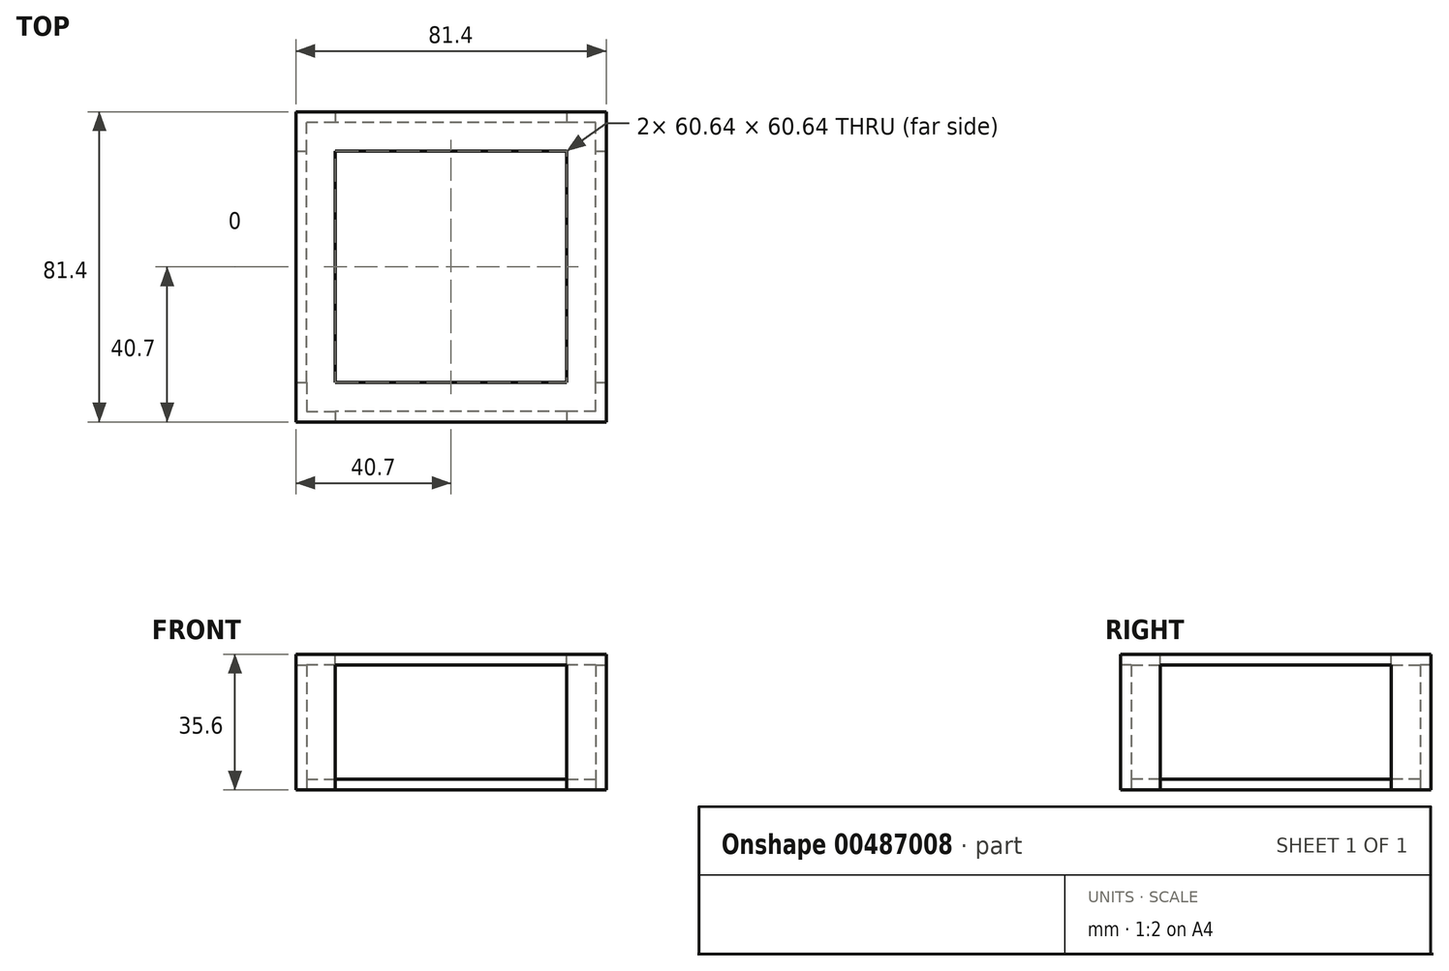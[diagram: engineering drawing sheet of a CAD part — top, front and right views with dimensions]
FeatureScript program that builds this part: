
annotation { "Feature Type Name" : "Feature", "Feature Type Description" : "" }
export const myFeature = defineFeature(function(context is Context, id is Id, definition is map)
    precondition{}
    {
        {
            assignVariable(context, id + "F0", {"name" : "Grosor", "anyValue" : 2.8});
        }
        {
            assignVariable(context, id + "F1", {"name" : "Alto", "anyValue" : 30});
        }
        {
            var Q0;
            Q0=qCreatedBy(makeId("Top.planeOp"),FACE);
            var sketch = newSketch(context, id + "F2", { "sketchPlane" : qUnion([Q0])});
            skLineSegment(sketch, "E0.bottom", {"start": v(37.9, -37.9) * mm, "end": v(-37.9, -37.9) * mm});
            skLineSegment(sketch, "E0.top", {"start": v(37.9, 37.9) * mm, "end": v(-37.9, 37.9) * mm});
            skLineSegment(sketch, "E0.left", {"start": v(37.9, -37.9) * mm, "end": v(37.9, 37.9) * mm});
            skLineSegment(sketch, "E0.right", {"start": v(-37.9, -37.9) * mm, "end": v(-37.9, 37.9) * mm});
            skPoint(sketch, "E0.middle", {"position": v(0, 0) * mm});
            skLineSegment(sketch, "E1.0", {"start": v(40.7, 40.7) * mm, "end": v(-40.7, 40.7) * mm});
            skLineSegment(sketch, "E1.1", {"start": v(40.7, -40.7) * mm, "end": v(40.7, 40.7) * mm});
            skLineSegment(sketch, "E1.2", {"start": v(40.7, -40.7) * mm, "end": v(-40.7, -40.7) * mm});
            skLineSegment(sketch, "E1.3", {"start": v(-40.7, -40.7) * mm, "end": v(-40.7, 40.7) * mm});
            skLineSegment(sketch, "E2.bottom", {"start": v(-30.32, 40.7) * mm, "end": v(30.32, 40.7) * mm});
            skLineSegment(sketch, "E2.top", {"start": v(-30.32, -40.7) * mm, "end": v(30.32, -40.7) * mm});
            skLineSegment(sketch, "E2.left", {"start": v(-30.32, 40.7) * mm, "end": v(-30.32, -40.7) * mm});
            skLineSegment(sketch, "E2.right", {"start": v(30.32, 40.7) * mm, "end": v(30.32, -40.7) * mm});
            skLineSegment(sketch, "E3.bottom", {"start": v(-40.7, 30.32) * mm, "end": v(40.7, 30.32) * mm});
            skLineSegment(sketch, "E3.top", {"start": v(-40.7, -30.32) * mm, "end": v(40.7, -30.32) * mm});
            skLineSegment(sketch, "E3.left", {"start": v(-40.7, 30.32) * mm, "end": v(-40.7, -30.32) * mm});
            skLineSegment(sketch, "E3.right", {"start": v(40.7, 30.32) * mm, "end": v(40.7, -30.32) * mm});
            skSolve(sketch);
        }
        {
            var Q0;
            {var subQ5=sQuery(id+"F2.wireOp",EDGE,"E2.bottom");Q0=makeQuery(id+"F2.imprint","IMPRINT",FACE,{"disambiguationData":[TD([[makeQuery(id+"F2.imprint","IMPRINT",EDGE,{"derivedFrom":subQ5}),-1.0]])]});}
            var Q1;
            {var subQ7=sQuery(id+"F2.wireOp",EDGE,"E0.right");var subQ8=sQuery(id+"F2.wireOp",EDGE,"E0.top");var subQ9=makeQuery(id+"F2.imprint","INTERSECT",VERTEX,{"derivedFrom":[subQ8,subQ7]});Q1=makeQuery(id+"F2.imprint","IMPRINT",FACE,{"disambiguationData":[TD([[makeQuery(id+"F2.imprint","IMPRINT",EDGE,{"disambiguationData":[TD([[subQ9,1.0]])],"derivedFrom":subQ8}),-1.0]])]});}
            var Q2;
            {var subQ7=sQuery(id+"F2.wireOp",EDGE,"E0.left");var subQ8=sQuery(id+"F2.wireOp",EDGE,"E0.top");var subQ9=makeQuery(id+"F2.imprint","INTERSECT",VERTEX,{"derivedFrom":[subQ8,subQ7]});Q2=makeQuery(id+"F2.imprint","IMPRINT",FACE,{"disambiguationData":[TD([[makeQuery(id+"F2.imprint","IMPRINT",EDGE,{"disambiguationData":[TD([[subQ9,-1.0]])],"derivedFrom":subQ8}),-1.0]])]});}
            var Q3;
            {var subQ5=sQuery(id+"F2.wireOp",EDGE,"E3.right");Q3=makeQuery(id+"F2.imprint","IMPRINT",FACE,{"disambiguationData":[TD([[makeQuery(id+"F2.imprint","IMPRINT",EDGE,{"derivedFrom":subQ5}),-1.0]])]});}
            var Q4;
            {var subQ7=sQuery(id+"F2.wireOp",EDGE,"E0.left");var subQ8=sQuery(id+"F2.wireOp",EDGE,"E0.bottom");var subQ9=makeQuery(id+"F2.imprint","INTERSECT",VERTEX,{"derivedFrom":[subQ8,subQ7]});Q4=makeQuery(id+"F2.imprint","IMPRINT",FACE,{"disambiguationData":[TD([[makeQuery(id+"F2.imprint","IMPRINT",EDGE,{"disambiguationData":[TD([[subQ9,-1.0]])],"derivedFrom":subQ8}),1.0]])]});}
            var Q5;
            {var subQ5=sQuery(id+"F2.wireOp",EDGE,"E2.top");Q5=makeQuery(id+"F2.imprint","IMPRINT",FACE,{"disambiguationData":[TD([[makeQuery(id+"F2.imprint","IMPRINT",EDGE,{"derivedFrom":subQ5}),1.0]])]});}
            var Q6;
            {var subQ5=sQuery(id+"F2.wireOp",EDGE,"E0.right");var subQ6=sQuery(id+"F2.wireOp",EDGE,"E0.bottom");var subQ7=makeQuery(id+"F2.imprint","INTERSECT",VERTEX,{"derivedFrom":[subQ6,subQ5]});Q6=makeQuery(id+"F2.imprint","IMPRINT",FACE,{"disambiguationData":[TD([[makeQuery(id+"F2.imprint","IMPRINT",EDGE,{"disambiguationData":[TD([[subQ7,1.0]])],"derivedFrom":subQ6}),1.0]])]});}
            var Q7;
            {var subQ5=sQuery(id+"F2.wireOp",EDGE,"E3.left");Q7=makeQuery(id+"F2.imprint","IMPRINT",FACE,{"disambiguationData":[TD([[makeQuery(id+"F2.imprint","IMPRINT",EDGE,{"derivedFrom":subQ5}),1.0]])]});}
            var Q8;
            {var subQ0=sQuery(id+"F2.wireOp",EDGE,"E0.left");var subQ1=sQuery(id+"F2.wireOp",EDGE,"E0.bottom");var subQ2=makeQuery(id+"F2.imprint","INTERSECT",VERTEX,{"derivedFrom":[subQ1,subQ0]});Q8=makeQuery(id+"F2.imprint","IMPRINT",FACE,{"disambiguationData":[TD([[makeQuery(id+"F2.imprint","IMPRINT",EDGE,{"disambiguationData":[TD([[subQ2,-1.0]])],"derivedFrom":subQ1}),-1.0]])]});}
            var Q9;
            {var subQ0=sQuery(id+"F2.wireOp",EDGE,"E0.left");var subQ1=sQuery(id+"F2.wireOp",EDGE,"E0.top");var subQ2=makeQuery(id+"F2.imprint","INTERSECT",VERTEX,{"derivedFrom":[subQ1,subQ0]});Q9=makeQuery(id+"F2.imprint","IMPRINT",FACE,{"disambiguationData":[TD([[makeQuery(id+"F2.imprint","IMPRINT",EDGE,{"disambiguationData":[TD([[subQ2,-1.0]])],"derivedFrom":subQ1}),1.0]])]});}
            var Q10;
            {var subQ0=sQuery(id+"F2.wireOp",EDGE,"E0.right");var subQ1=sQuery(id+"F2.wireOp",EDGE,"E0.top");var subQ2=makeQuery(id+"F2.imprint","INTERSECT",VERTEX,{"derivedFrom":[subQ1,subQ0]});Q10=makeQuery(id+"F2.imprint","IMPRINT",FACE,{"disambiguationData":[TD([[makeQuery(id+"F2.imprint","IMPRINT",EDGE,{"disambiguationData":[TD([[subQ2,1.0]])],"derivedFrom":subQ1}),1.0]])]});}
            var Q11;
            {var subQ0=sQuery(id+"F2.wireOp",EDGE,"E3.top");var subQ1=sQuery(id+"F2.wireOp",EDGE,"E0.right");var subQ2=makeQuery(id+"F2.imprint","INTERSECT",VERTEX,{"derivedFrom":[subQ1,subQ0]});Q11=makeQuery(id+"F2.imprint","IMPRINT",FACE,{"disambiguationData":[TD([[makeQuery(id+"F2.imprint","IMPRINT",EDGE,{"disambiguationData":[TD([[subQ2,-1.0]])],"derivedFrom":subQ1}),-1.0]])]});}
            var Q12;
            {var subQ0=sQuery(id+"F2.wireOp",EDGE,"E3.top");var subQ1=sQuery(id+"F2.wireOp",EDGE,"E0.left");var subQ2=makeQuery(id+"F2.imprint","INTERSECT",VERTEX,{"derivedFrom":[subQ1,subQ0]});Q12=makeQuery(id+"F2.imprint","IMPRINT",FACE,{"disambiguationData":[TD([[makeQuery(id+"F2.imprint","IMPRINT",EDGE,{"disambiguationData":[TD([[subQ2,-1.0]])],"derivedFrom":subQ1}),1.0]])]});}
            var Q13;
            {var subQ0=sQuery(id+"F2.wireOp",EDGE,"E0.right");var subQ1=sQuery(id+"F2.wireOp",EDGE,"E0.bottom");var subQ2=makeQuery(id+"F2.imprint","INTERSECT",VERTEX,{"derivedFrom":[subQ1,subQ0]});Q13=makeQuery(id+"F2.imprint","IMPRINT",FACE,{"disambiguationData":[TD([[makeQuery(id+"F2.imprint","IMPRINT",EDGE,{"disambiguationData":[TD([[subQ2,1.0]])],"derivedFrom":subQ1}),-1.0]])]});}
            var Q14;
            {var subQ0=sQuery(id+"F2.wireOp",EDGE,"E2.right");var subQ1=sQuery(id+"F2.wireOp",EDGE,"E0.bottom");var subQ2=makeQuery(id+"F2.imprint","INTERSECT",VERTEX,{"derivedFrom":[subQ1,subQ0]});Q14=makeQuery(id+"F2.imprint","IMPRINT",FACE,{"disambiguationData":[TD([[makeQuery(id+"F2.imprint","IMPRINT",EDGE,{"disambiguationData":[TD([[subQ2,-1.0]])],"derivedFrom":subQ1}),-1.0]])]});}
            var Q15;
            {var subQ0=sQuery(id+"F2.wireOp",EDGE,"E2.right");var subQ1=sQuery(id+"F2.wireOp",EDGE,"E0.top");var subQ2=makeQuery(id+"F2.imprint","INTERSECT",VERTEX,{"derivedFrom":[subQ1,subQ0]});Q15=makeQuery(id+"F2.imprint","IMPRINT",FACE,{"disambiguationData":[TD([[makeQuery(id+"F2.imprint","IMPRINT",EDGE,{"disambiguationData":[TD([[subQ2,-1.0]])],"derivedFrom":subQ1}),1.0]])]});}
            extrude(context, id + "F3", {"entities" : qUnion([Q0, Q1, Q2, Q3, Q4, Q5, Q6, Q7, Q8, Q9, Q10, Q11, Q12, Q13, Q14, Q15]), "depth" : (getVariable(context, 'Grosor')) * mm});
        }
        {
            var Q0;
            {var subQ5=sQuery(id+"F2.wireOp",EDGE,"E2.bottom");Q0=makeQuery(id+"F2.imprint","IMPRINT",FACE,{"disambiguationData":[TD([[makeQuery(id+"F2.imprint","IMPRINT",EDGE,{"derivedFrom":subQ5}),-1.0]])]});}
            var Q1;
            {var subQ7=sQuery(id+"F2.wireOp",EDGE,"E0.right");var subQ8=sQuery(id+"F2.wireOp",EDGE,"E0.top");var subQ9=makeQuery(id+"F2.imprint","INTERSECT",VERTEX,{"derivedFrom":[subQ8,subQ7]});Q1=makeQuery(id+"F2.imprint","IMPRINT",FACE,{"disambiguationData":[TD([[makeQuery(id+"F2.imprint","IMPRINT",EDGE,{"disambiguationData":[TD([[subQ9,1.0]])],"derivedFrom":subQ8}),-1.0]])]});}
            var Q2;
            {var subQ5=sQuery(id+"F2.wireOp",EDGE,"E3.left");Q2=makeQuery(id+"F2.imprint","IMPRINT",FACE,{"disambiguationData":[TD([[makeQuery(id+"F2.imprint","IMPRINT",EDGE,{"derivedFrom":subQ5}),1.0]])]});}
            var Q3;
            {var subQ5=sQuery(id+"F2.wireOp",EDGE,"E0.right");var subQ6=sQuery(id+"F2.wireOp",EDGE,"E0.bottom");var subQ7=makeQuery(id+"F2.imprint","INTERSECT",VERTEX,{"derivedFrom":[subQ6,subQ5]});Q3=makeQuery(id+"F2.imprint","IMPRINT",FACE,{"disambiguationData":[TD([[makeQuery(id+"F2.imprint","IMPRINT",EDGE,{"disambiguationData":[TD([[subQ7,1.0]])],"derivedFrom":subQ6}),1.0]])]});}
            var Q4;
            {var subQ5=sQuery(id+"F2.wireOp",EDGE,"E2.top");Q4=makeQuery(id+"F2.imprint","IMPRINT",FACE,{"disambiguationData":[TD([[makeQuery(id+"F2.imprint","IMPRINT",EDGE,{"derivedFrom":subQ5}),1.0]])]});}
            var Q5;
            {var subQ7=sQuery(id+"F2.wireOp",EDGE,"E0.left");var subQ8=sQuery(id+"F2.wireOp",EDGE,"E0.bottom");var subQ9=makeQuery(id+"F2.imprint","INTERSECT",VERTEX,{"derivedFrom":[subQ8,subQ7]});Q5=makeQuery(id+"F2.imprint","IMPRINT",FACE,{"disambiguationData":[TD([[makeQuery(id+"F2.imprint","IMPRINT",EDGE,{"disambiguationData":[TD([[subQ9,-1.0]])],"derivedFrom":subQ8}),1.0]])]});}
            var Q6;
            {var subQ5=sQuery(id+"F2.wireOp",EDGE,"E3.right");Q6=makeQuery(id+"F2.imprint","IMPRINT",FACE,{"disambiguationData":[TD([[makeQuery(id+"F2.imprint","IMPRINT",EDGE,{"derivedFrom":subQ5}),-1.0]])]});}
            var Q7;
            {var subQ7=sQuery(id+"F2.wireOp",EDGE,"E0.left");var subQ8=sQuery(id+"F2.wireOp",EDGE,"E0.top");var subQ9=makeQuery(id+"F2.imprint","INTERSECT",VERTEX,{"derivedFrom":[subQ8,subQ7]});Q7=makeQuery(id+"F2.imprint","IMPRINT",FACE,{"disambiguationData":[TD([[makeQuery(id+"F2.imprint","IMPRINT",EDGE,{"disambiguationData":[TD([[subQ9,-1.0]])],"derivedFrom":subQ8}),-1.0]])]});}
            extrude(context, id + "F4", {"entities" : qUnion([Q0, Q1, Q2, Q3, Q4, Q5, Q6, Q7]), "operationType" : NewBodyOperationType.ADD, "depth" : (getVariable(context, 'Alto') / 5) * mm});
        }
        {
            var Q0;
            {var subQ7=sQuery(id+"F2.wireOp",EDGE,"E0.right");var subQ8=sQuery(id+"F2.wireOp",EDGE,"E0.top");var subQ9=makeQuery(id+"F2.imprint","INTERSECT",VERTEX,{"derivedFrom":[subQ8,subQ7]});Q0=makeQuery(id+"F2.imprint","IMPRINT",FACE,{"disambiguationData":[TD([[makeQuery(id+"F2.imprint","IMPRINT",EDGE,{"disambiguationData":[TD([[subQ9,1.0]])],"derivedFrom":subQ8}),-1.0]])]});}
            var Q1;
            {var subQ7=sQuery(id+"F2.wireOp",EDGE,"E0.left");var subQ8=sQuery(id+"F2.wireOp",EDGE,"E0.top");var subQ9=makeQuery(id+"F2.imprint","INTERSECT",VERTEX,{"derivedFrom":[subQ8,subQ7]});Q1=makeQuery(id+"F2.imprint","IMPRINT",FACE,{"disambiguationData":[TD([[makeQuery(id+"F2.imprint","IMPRINT",EDGE,{"disambiguationData":[TD([[subQ9,-1.0]])],"derivedFrom":subQ8}),-1.0]])]});}
            var Q2;
            {var subQ7=sQuery(id+"F2.wireOp",EDGE,"E0.left");var subQ8=sQuery(id+"F2.wireOp",EDGE,"E0.bottom");var subQ9=makeQuery(id+"F2.imprint","INTERSECT",VERTEX,{"derivedFrom":[subQ8,subQ7]});Q2=makeQuery(id+"F2.imprint","IMPRINT",FACE,{"disambiguationData":[TD([[makeQuery(id+"F2.imprint","IMPRINT",EDGE,{"disambiguationData":[TD([[subQ9,-1.0]])],"derivedFrom":subQ8}),1.0]])]});}
            var Q3;
            {var subQ5=sQuery(id+"F2.wireOp",EDGE,"E0.right");var subQ6=sQuery(id+"F2.wireOp",EDGE,"E0.bottom");var subQ7=makeQuery(id+"F2.imprint","INTERSECT",VERTEX,{"derivedFrom":[subQ6,subQ5]});Q3=makeQuery(id+"F2.imprint","IMPRINT",FACE,{"disambiguationData":[TD([[makeQuery(id+"F2.imprint","IMPRINT",EDGE,{"disambiguationData":[TD([[subQ7,1.0]])],"derivedFrom":subQ6}),1.0]])]});}
            extrude(context, id + "F5", {"entities" : qUnion([Q0, Q1, Q2, Q3]), "operationType" : NewBodyOperationType.ADD, "depth" : (getVariable(context, 'Alto') + (getVariable(context, 'Grosor') * 2)) * mm});
        }
        {
            var Q0;
            Q0=makeQuery(id+"F5.opExtrude","CAP_FACE",FACE,{"disambiguationData":[OSD([sQuery(id+"F2.wireOp",EDGE,"E0.top"),sQuery(id+"F2.wireOp",EDGE,"E0.right"),sQuery(id+"F2.wireOp",EDGE,"E1.0"),sQuery(id+"F2.wireOp",EDGE,"E1.3"),sQuery(id+"F2.wireOp",EDGE,"E2.left"),sQuery(id+"F2.wireOp",EDGE,"E3.bottom")])],"isStart":false});
            cPlane(context, id + "F6", {"entities" : qUnion([Q0]), "cplaneType" : CPlaneType.OFFSET, "offset" : 0 * mm, "width" : 150 * mm, "height" : 150 * mm});
        }
        {
            var Q0;
            Q0=qCreatedBy(id+"F6.planeOp",FACE);
            var sketch = newSketch(context, id + "F7", { "sketchPlane" : qUnion([Q0])});
            skLineSegment(sketch, "E4.bottom", {"start": v(37.9, -37.9) * mm, "end": v(-37.9, -37.9) * mm});
            skLineSegment(sketch, "E4.top", {"start": v(37.9, 37.9) * mm, "end": v(-37.9, 37.9) * mm});
            skLineSegment(sketch, "E4.left", {"start": v(37.9, -37.9) * mm, "end": v(37.9, 37.9) * mm});
            skLineSegment(sketch, "E4.right", {"start": v(-37.9, -37.9) * mm, "end": v(-37.9, 37.9) * mm});
            skPoint(sketch, "E4.middle", {"position": v(0, 0) * mm});
            skLineSegment(sketch, "E5.0", {"start": v(40.7, 40.7) * mm, "end": v(-40.7, 40.7) * mm});
            skLineSegment(sketch, "E5.1", {"start": v(40.7, -40.7) * mm, "end": v(40.7, 40.7) * mm});
            skLineSegment(sketch, "E5.2", {"start": v(40.7, -40.7) * mm, "end": v(-40.7, -40.7) * mm});
            skLineSegment(sketch, "E5.3", {"start": v(-40.7, -40.7) * mm, "end": v(-40.7, 40.7) * mm});
            skLineSegment(sketch, "E6.bottom", {"start": v(-30.32, 40.7) * mm, "end": v(30.32, 40.7) * mm});
            skLineSegment(sketch, "E6.top", {"start": v(-30.32, -40.7) * mm, "end": v(30.32, -40.7) * mm});
            skLineSegment(sketch, "E6.left", {"start": v(-30.32, 40.7) * mm, "end": v(-30.32, -40.7) * mm});
            skLineSegment(sketch, "E6.right", {"start": v(30.32, 40.7) * mm, "end": v(30.32, -40.7) * mm});
            skLineSegment(sketch, "E7.bottom", {"start": v(-40.7, 30.32) * mm, "end": v(40.7, 30.32) * mm});
            skLineSegment(sketch, "E7.top", {"start": v(-40.7, -30.32) * mm, "end": v(40.7, -30.32) * mm});
            skLineSegment(sketch, "E7.left", {"start": v(-40.7, 30.32) * mm, "end": v(-40.7, -30.32) * mm});
            skLineSegment(sketch, "E7.right", {"start": v(40.7, 30.32) * mm, "end": v(40.7, -30.32) * mm});
            skSolve(sketch);
        }
        {
            var Q0;
            Q0 = qSketchRegion(id + "F7", true);
            var Q1;
            {var subQ0=sQuery(id+"F7.wireOp",EDGE,"E6.right");var subQ1=sQuery(id+"F7.wireOp",EDGE,"E4.top");var subQ2=makeQuery(id+"F7.imprint","INTERSECT",VERTEX,{"derivedFrom":[subQ1,subQ0]});Q1=makeQuery(id+"F7.imprint","IMPRINT",FACE,{"disambiguationData":[TD([[makeQuery(id+"F7.imprint","IMPRINT",EDGE,{"disambiguationData":[TD([[subQ2,-1.0]])],"derivedFrom":subQ1}),1.0]])]});}
            var Q2;
            {var subQ0=sQuery(id+"F7.wireOp",EDGE,"E4.left");var subQ1=sQuery(id+"F7.wireOp",EDGE,"E4.top");var subQ2=makeQuery(id+"F7.imprint","INTERSECT",VERTEX,{"derivedFrom":[subQ1,subQ0]});Q2=makeQuery(id+"F7.imprint","IMPRINT",FACE,{"disambiguationData":[TD([[makeQuery(id+"F7.imprint","IMPRINT",EDGE,{"disambiguationData":[TD([[subQ2,-1.0]])],"derivedFrom":subQ1}),1.0]])]});}
            var Q3;
            {var subQ0=sQuery(id+"F7.wireOp",EDGE,"E7.top");var subQ1=sQuery(id+"F7.wireOp",EDGE,"E4.left");var subQ2=makeQuery(id+"F7.imprint","INTERSECT",VERTEX,{"derivedFrom":[subQ1,subQ0]});Q3=makeQuery(id+"F7.imprint","IMPRINT",FACE,{"disambiguationData":[TD([[makeQuery(id+"F7.imprint","IMPRINT",EDGE,{"disambiguationData":[TD([[subQ2,-1.0]])],"derivedFrom":subQ1}),1.0]])]});}
            var Q4;
            {var subQ0=sQuery(id+"F7.wireOp",EDGE,"E4.left");var subQ1=sQuery(id+"F7.wireOp",EDGE,"E4.bottom");var subQ2=makeQuery(id+"F7.imprint","INTERSECT",VERTEX,{"derivedFrom":[subQ1,subQ0]});Q4=makeQuery(id+"F7.imprint","IMPRINT",FACE,{"disambiguationData":[TD([[makeQuery(id+"F7.imprint","IMPRINT",EDGE,{"disambiguationData":[TD([[subQ2,-1.0]])],"derivedFrom":subQ1}),-1.0]])]});}
            var Q5;
            {var subQ0=sQuery(id+"F7.wireOp",EDGE,"E6.right");var subQ1=sQuery(id+"F7.wireOp",EDGE,"E4.bottom");var subQ2=makeQuery(id+"F7.imprint","INTERSECT",VERTEX,{"derivedFrom":[subQ1,subQ0]});Q5=makeQuery(id+"F7.imprint","IMPRINT",FACE,{"disambiguationData":[TD([[makeQuery(id+"F7.imprint","IMPRINT",EDGE,{"disambiguationData":[TD([[subQ2,-1.0]])],"derivedFrom":subQ1}),-1.0]])]});}
            var Q6;
            {var subQ0=sQuery(id+"F7.wireOp",EDGE,"E4.right");var subQ1=sQuery(id+"F7.wireOp",EDGE,"E4.bottom");var subQ2=makeQuery(id+"F7.imprint","INTERSECT",VERTEX,{"derivedFrom":[subQ1,subQ0]});Q6=makeQuery(id+"F7.imprint","IMPRINT",FACE,{"disambiguationData":[TD([[makeQuery(id+"F7.imprint","IMPRINT",EDGE,{"disambiguationData":[TD([[subQ2,1.0]])],"derivedFrom":subQ1}),-1.0]])]});}
            var Q7;
            {var subQ0=sQuery(id+"F7.wireOp",EDGE,"E7.top");var subQ1=sQuery(id+"F7.wireOp",EDGE,"E4.right");var subQ2=makeQuery(id+"F7.imprint","INTERSECT",VERTEX,{"derivedFrom":[subQ1,subQ0]});Q7=makeQuery(id+"F7.imprint","IMPRINT",FACE,{"disambiguationData":[TD([[makeQuery(id+"F7.imprint","IMPRINT",EDGE,{"disambiguationData":[TD([[subQ2,-1.0]])],"derivedFrom":subQ1}),-1.0]])]});}
            var Q8;
            {var subQ0=sQuery(id+"F7.wireOp",EDGE,"E4.right");var subQ1=sQuery(id+"F7.wireOp",EDGE,"E4.top");var subQ2=makeQuery(id+"F7.imprint","INTERSECT",VERTEX,{"derivedFrom":[subQ1,subQ0]});Q8=makeQuery(id+"F7.imprint","IMPRINT",FACE,{"disambiguationData":[TD([[makeQuery(id+"F7.imprint","IMPRINT",EDGE,{"disambiguationData":[TD([[subQ2,1.0]])],"derivedFrom":subQ1}),1.0]])]});}
            extrude(context, id + "F8", {"entities" : qUnion([Q0, Q1, Q2, Q3, Q4, Q5, Q6, Q7, Q8]), "operationType" : NewBodyOperationType.ADD, "oppositeDirection" : true, "depth" : (getVariable(context, 'Grosor')) * mm});
        }
        {
            var Q0;
            {var subQ5=sQuery(id+"F7.wireOp",EDGE,"E4.right");var subQ6=sQuery(id+"F7.wireOp",EDGE,"E4.bottom");var subQ7=makeQuery(id+"F7.imprint","INTERSECT",VERTEX,{"derivedFrom":[subQ6,subQ5]});Q0=makeQuery(id+"F7.imprint","IMPRINT",FACE,{"disambiguationData":[TD([[makeQuery(id+"F7.imprint","IMPRINT",EDGE,{"disambiguationData":[TD([[subQ7,1.0]])],"derivedFrom":subQ6}),1.0]])]});}
            var Q1;
            {var subQ5=sQuery(id+"F7.wireOp",EDGE,"E7.left");Q1=makeQuery(id+"F7.imprint","IMPRINT",FACE,{"disambiguationData":[TD([[makeQuery(id+"F7.imprint","IMPRINT",EDGE,{"derivedFrom":subQ5}),1.0]])]});}
            var Q2;
            {var subQ5=sQuery(id+"F7.wireOp",EDGE,"E6.top");Q2=makeQuery(id+"F7.imprint","IMPRINT",FACE,{"disambiguationData":[TD([[makeQuery(id+"F7.imprint","IMPRINT",EDGE,{"derivedFrom":subQ5}),1.0]])]});}
            var Q3;
            {var subQ5=sQuery(id+"F7.wireOp",EDGE,"E7.right");Q3=makeQuery(id+"F7.imprint","IMPRINT",FACE,{"disambiguationData":[TD([[makeQuery(id+"F7.imprint","IMPRINT",EDGE,{"derivedFrom":subQ5}),-1.0]])]});}
            var Q4;
            {var subQ5=sQuery(id+"F7.wireOp",EDGE,"E6.bottom");Q4=makeQuery(id+"F7.imprint","IMPRINT",FACE,{"disambiguationData":[TD([[makeQuery(id+"F7.imprint","IMPRINT",EDGE,{"derivedFrom":subQ5}),-1.0]])]});}
            extrude(context, id + "F9", {"entities" : qUnion([Q0, Q1, Q2, Q3, Q4]), "operationType" : NewBodyOperationType.ADD, "oppositeDirection" : true, "depth" : (getVariable(context, 'Alto') / 5) * mm});
        }
    });
